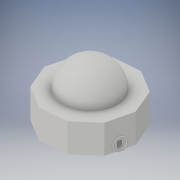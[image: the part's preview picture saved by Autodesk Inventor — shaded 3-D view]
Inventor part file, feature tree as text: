
AUTODESK INVENTOR PART (.ipt)
format: ipt  version: 2017 (Build 210142000, 142)  size: 251,904 bytes
history: native  units: in
note: dims shown in document units (in); Inventor stores cm internally (conversion verified against a paired STEP export)
features: sketch x7, extrude x6, other x3, mirror x1
ambient origin geometry x8: Origin, YZ Plane, XZ Plane, XY Plane, X Axis, Y Axis, Z Axis, Center Point
bodies: Solid1 (feature_tree)
feature tree (17):
  other  "dome"
  extrude  "bace"  Depth=1.0in TaperAngle=0.0deg
  extrude  "bace wall"  Depth=20.0in TaperAngle=0.0deg
  extrude  "bace cieiling"  Depth=6.6667in
  other  "dome work plane"
  extrude  "door frame"  Depth=1.0in TaperAngle=0.0deg
  extrude  "corridor connection"  Depth=0.25in
  extrude  "left door slot"  Depth=2.0in
  other  "door slot mirror"
  mirror  "Mirror1"
  sketch  "Sketch1"  dims[d0=62.0in d1=1.0in d2=0.0in]
  sketch  "Sketch2"  dims[d4=1.0in d5=20.0in d6=0.0in]
  sketch  "Sketch3"  dims[d8=1.0in d9=0.0in d14=6.6667in d15=4.0in]
  sketch  "Sketch7"  dims[d16=2.0in d17=6.6667in d18=1.0in d19=0.0in]
  sketch  "Sketch8"  dims[d20=1.0in d21=0.0in d22=0.25in d23=0.5in d24=6.6667in]
  sketch  "Sketch9"  dims[d25=2.0in d26=0.0in d28=40.0in]
  sketch  "Sketch10"  dims[d32=20.0in d33=21.0in d34=90.0deg]
